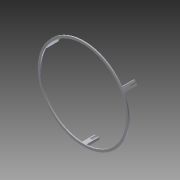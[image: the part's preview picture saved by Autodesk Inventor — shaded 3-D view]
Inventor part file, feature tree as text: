
AUTODESK INVENTOR PART (.ipt)
format: ipt  version: 2014 (Build 180170000, 170)  size: 249,344 bytes
history: native  units: mm
features: extrude x5, sketch x5
ambient origin geometry x8: Origin, YZ Plane, XZ Plane, XY Plane, X Axis, Y Axis, Z Axis, Center Point
bodies: Solid1 (feature_tree)
feature tree (10):
  extrude  "Extrusion1"  Depth=75.0mm
  extrude  "Extrusion2"  Depth=1.0mm
  extrude  "Extrusion3"  Depth=0.74mm
  extrude  "Extrusion4"  TaperAngle=45.0deg  [1 undecoded]
  extrude  "Extrusion5"  Depth=6.0mm
  sketch  "Sketch1"  dims[d0=79.0mm d1=75.0mm]
  sketch  "Sketch2"  dims[d2=1.0mm d3=0.0mm d4=1.31mm]
  sketch  "Sketch3"  dims[d5=0.74mm d6=0.76mm]
  sketch  "Sketch4"  dims[d7=0.74mm d8=45.0deg]
  sketch  "Sketch5"  dims[d9=0.75mm d10=0.523599mm d11=0.523599mm d12=1.0mm d13=30.0mm d15=360.0deg d17=11.0mm d18=0.0mm d19=6.0mm d20=0.0mm d21=6.0mm d22=0.0mm d23=6.0mm d24=0.0mm]
note: 1 required parameter value undecoded (feature->parameter linkage not recoverable at this tier; creation-order binding heuristic only, values carry confidence <= 0.55)
